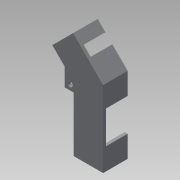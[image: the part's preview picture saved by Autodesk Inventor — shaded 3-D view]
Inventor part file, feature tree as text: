
AUTODESK INVENTOR PART (.ipt)
format: ipt  version: 2015 SP1 (Build 190203100, 203)  size: 107,008 bytes
history: native  units: mm
features: extrude x2, sketch x2
ambient origin geometry x8: Origin, YZ Plane, XZ Plane, XY Plane, X Axis, Y Axis, Z Axis, Center Point
bodies: Solid1 (feature_tree)
feature tree (4):
  extrude  "Extrusion1"  Depth=15.0mm
  extrude  "Extrusion2"  Depth=15.0mm
  sketch  "Sketch1"  dims[d4=2.0mm d5=0.0mm d6=15.0mm]
  sketch  "Sketch2"  dims[d7=2.0mm d8=15.0mm d9=2.0mm d10=90.0deg d11=90.0deg d12=15.0mm d13=7.5mm d14=45.0deg d15=2.0mm d16=15.0mm d17=0.0mm]
